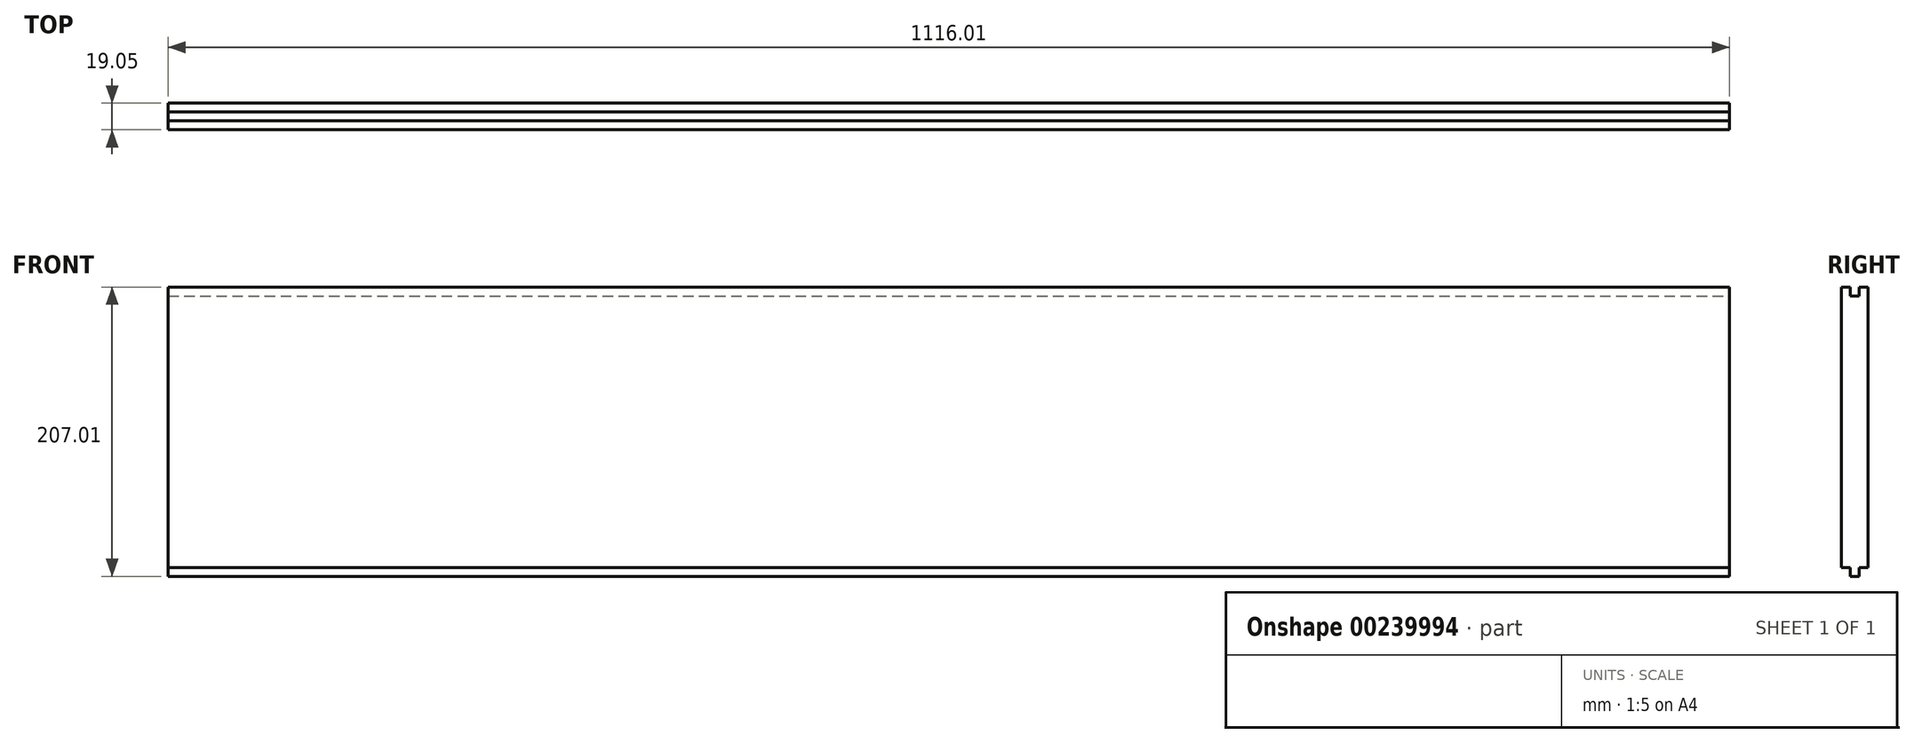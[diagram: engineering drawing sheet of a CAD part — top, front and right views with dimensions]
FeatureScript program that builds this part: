
annotation { "Feature Type Name" : "Feature", "Feature Type Description" : "" }
export const myFeature = defineFeature(function(context is Context, id is Id, definition is map)
    precondition{}
    {
        {
            var Q0;
            Q0=qCreatedBy(makeId("Front.planeOp"),FACE);
            var sketch = newSketch(context, id + "F0", { "sketchPlane" : qUnion([Q0])});
            skLineSegment(sketch, "E0.bottom", {"start": v(-599.98, -295.78) * mm, "end": v(516.03, -295.78) * mm});
            skLineSegment(sketch, "E0.top", {"start": v(-599.98, -502.8) * mm, "end": v(516.03, -502.8) * mm});
            skLineSegment(sketch, "E0.left", {"start": v(-599.98, -295.78) * mm, "end": v(-599.98, -502.8) * mm});
            skLineSegment(sketch, "E0.right", {"start": v(516.03, -295.78) * mm, "end": v(516.03, -502.8) * mm});
            skSolve(sketch);
        }
        {
            var Q0;
            Q0=makeQuery(id+"F0.imprint","IMPRINT",FACE,{"disambiguationData":[TD([[makeQuery(id+"F0.imprint","IMPRINT",EDGE,{"derivedFrom":sQuery(id+"F0.wireOp",EDGE,"E0.bottom")}),-1.0]])]});
            extrude(context, id + "F1", {"entities" : qUnion([Q0]), "depth" : 19.05 * mm, "offsetDistance" : 25.4 * mm});
        }
        {
            var Q0;
            Q0=makeQuery(id+"F1.opExtrude","SWEPT_FACE",FACE,{"disambiguationData":[OSD([sQuery(id+"F0.wireOp",EDGE,"E0.right")])]});
            var sketch = newSketch(context, id + "F2", { "sketchPlane" : qUnion([Q0])});
            skLineSegment(sketch, "E1.bottom", {"start": v(-12.7, -295.78) * mm, "end": v(-6.35, -295.78) * mm});
            skLineSegment(sketch, "E1.top", {"start": v(-12.7, -302.13) * mm, "end": v(-6.35, -302.13) * mm});
            skLineSegment(sketch, "E1.left", {"start": v(-12.7, -295.78) * mm, "end": v(-12.7, -302.13) * mm});
            skLineSegment(sketch, "E1.right", {"start": v(-6.35, -295.78) * mm, "end": v(-6.35, -302.13) * mm});
            skSolve(sketch);
        }
        {
            var Q0;
            Q0=qSketchRegion(id+"F2",true);
            extrude(context, id + "F3", {"entities" : qUnion([Q0]), "operationType" : NewBodyOperationType.REMOVE, "endBound" : BoundingType.THROUGH_ALL, "oppositeDirection" : true, "depth" : 25.4 * mm, "offsetDistance" : 25.4 * mm});
        }
        {
            var Q0;
            Q0=makeQuery(id+"F1.opExtrude","SWEPT_FACE",FACE,{"disambiguationData":[OSD([sQuery(id+"F0.wireOp",EDGE,"E0.right")])]});
            var sketch = newSketch(context, id + "F4", { "sketchPlane" : qUnion([Q0])});
            skLineSegment(sketch, "E2.bottom", {"start": v(-19.05, -496.44) * mm, "end": v(-12.7, -496.44) * mm});
            skLineSegment(sketch, "E2.top", {"start": v(-19.05, -502.8) * mm, "end": v(-12.7, -502.8) * mm});
            skLineSegment(sketch, "E2.left", {"start": v(-19.05, -496.44) * mm, "end": v(-19.05, -502.8) * mm});
            skLineSegment(sketch, "E2.right", {"start": v(-12.7, -496.44) * mm, "end": v(-12.7, -502.8) * mm});
            skLineSegment(sketch, "E3.bottom", {"start": v(-6.35, -496.44) * mm, "end": v(0, -496.44) * mm});
            skLineSegment(sketch, "E3.top", {"start": v(-6.35, -502.8) * mm, "end": v(0, -502.8) * mm});
            skLineSegment(sketch, "E3.left", {"start": v(-6.35, -496.44) * mm, "end": v(-6.35, -502.8) * mm});
            skLineSegment(sketch, "E3.right", {"start": v(0, -496.44) * mm, "end": v(0, -502.8) * mm});
            skSolve(sketch);
        }
        {
            var Q0;
            Q0=makeQuery(id+"F4.imprint","IMPRINT",FACE,{"disambiguationData":[TD([[makeQuery(id+"F4.imprint","IMPRINT",EDGE,{"derivedFrom":sQuery(id+"F4.wireOp",EDGE,"E2.bottom")}),-1.0]])]});
            var Q1;
            Q1=makeQuery(id+"F4.imprint","IMPRINT",FACE,{"disambiguationData":[TD([[makeQuery(id+"F4.imprint","IMPRINT",EDGE,{"derivedFrom":sQuery(id+"F4.wireOp",EDGE,"E3.bottom")}),-1.0]])]});
            extrude(context, id + "F5", {"entities" : qUnion([Q0, Q1]), "operationType" : NewBodyOperationType.REMOVE, "endBound" : BoundingType.THROUGH_ALL, "oppositeDirection" : true, "depth" : 25.4 * mm, "offsetDistance" : 25.4 * mm});
        }
    });
